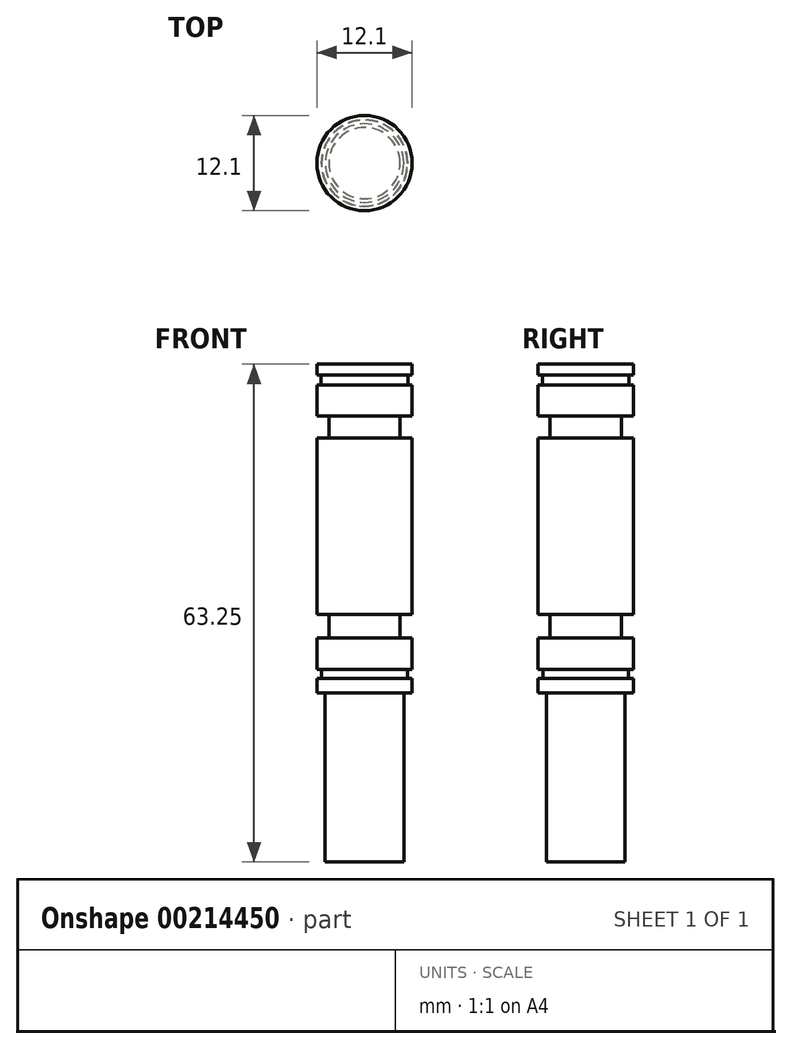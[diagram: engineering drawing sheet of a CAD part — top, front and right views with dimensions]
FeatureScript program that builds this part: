
annotation { "Feature Type Name" : "Feature", "Feature Type Description" : "" }
export const myFeature = defineFeature(function(context is Context, id is Id, definition is map)
    precondition{}
    {
        {
            var Q0;
            Q0=qCreatedBy(makeId("Top.planeOp"),FACE);
            var sketch = newSketch(context, id + "F0", { "sketchPlane" : qUnion([Q0])});
            skCircle(sketch, "E0", {"center": v(0, 0) * mm, "radius": 5 * mm});
            skSolve(sketch);
        }
        {
            var Q0;
            Q0=makeQuery(id+"F0.imprint","IMPRINT",FACE,{"disambiguationData":[TD([[makeQuery(id+"F0.imprint","IMPRINT",EDGE,{"derivedFrom":sQuery(id+"F0.wireOp",EDGE,"E0")}),1.0]])]});
            extrude(context, id + "F1", {"entities" : qUnion([Q0]), "oppositeDirection" : true, "depth" : 21.5 * mm});
        }
        {
            var Q0;
            Q0=qCreatedBy(makeId("Top.planeOp"),FACE);
            var sketch = newSketch(context, id + "F2", { "sketchPlane" : qUnion([Q0])});
            skCircle(sketch, "E1", {"center": v(0, 0) * mm, "radius": 6.05 * mm});
            skSolve(sketch);
        }
        {
            var Q0;
            Q0=makeQuery(id+"F2.imprint","IMPRINT",FACE,{"disambiguationData":[TD([[makeQuery(id+"F2.imprint","IMPRINT",EDGE,{"derivedFrom":sQuery(id+"F2.wireOp",EDGE,"E1")}),1.0]])]});
            var Q1;
            Q1=sQuery(id+"F2.wireOp",EDGE,"E1");
            extrude(context, id + "F3", {"entities" : qUnion([Q0]), "operationType" : NewBodyOperationType.ADD, "surfaceEntities" : qUnion([Q1]), "depth" : 1.8 * mm});
        }
        {
            var Q0;
            Q0=makeQuery(id+"F3.opExtrude","CAP_FACE",FACE,{"disambiguationData":[OSD([sQuery(id+"F2.wireOp",EDGE,"E1")])],"isStart":false});
            var sketch = newSketch(context, id + "F4", { "sketchPlane" : qUnion([Q0])});
            skCircle(sketch, "E2", {"center": v(0, 0) * mm, "radius": 5.45 * mm});
            skSolve(sketch);
        }
        {
            var Q0;
            Q0 = qSketchRegion(id + "F4", true);
            extrude(context, id + "F5", {"entities" : qUnion([Q0]), "operationType" : NewBodyOperationType.ADD, "depth" : 1.2 * mm});
        }
        {
            var Q0;
            Q0=makeQuery(id+"F5.opExtrude","CAP_FACE",FACE,{"disambiguationData":[OSD([sQuery(id+"F4.wireOp",EDGE,"E2")])],"isStart":false});
            var sketch = newSketch(context, id + "F6", { "sketchPlane" : qUnion([Q0])});
            skCircle(sketch, "E3", {"center": v(0, 0) * mm, "radius": 6.05 * mm});
            skSolve(sketch);
        }
        {
            var Q0;
            Q0 = qSketchRegion(id + "F6", true);
            extrude(context, id + "F7", {"entities" : qUnion([Q0]), "operationType" : NewBodyOperationType.ADD, "depth" : 3.95 * mm});
        }
        {
            var Q0;
            Q0=makeQuery(id+"F7.opExtrude","CAP_FACE",FACE,{"disambiguationData":[OSD([sQuery(id+"F6.wireOp",EDGE,"E3")])],"isStart":false});
            var sketch = newSketch(context, id + "F8", { "sketchPlane" : qUnion([Q0])});
            skCircle(sketch, "E4", {"center": v(0, 0) * mm, "radius": 4.53 * mm});
            skSolve(sketch);
        }
        {
            var Q0;
            Q0 = qSketchRegion(id + "F8", true);
            extrude(context, id + "F9", {"entities" : qUnion([Q0]), "operationType" : NewBodyOperationType.ADD, "depth" : 3 * mm});
        }
        {
            var Q0;
            Q0=makeQuery(id+"F9.opExtrude","CAP_FACE",FACE,{"disambiguationData":[OSD([sQuery(id+"F8.wireOp",EDGE,"E4")])],"isStart":false});
            var sketch = newSketch(context, id + "F10", { "sketchPlane" : qUnion([Q0])});
            skCircle(sketch, "E5", {"center": v(0, 0) * mm, "radius": 6.05 * mm});
            skSolve(sketch);
        }
        {
            var Q0;
            Q0 = qSketchRegion(id + "F10", true);
            extrude(context, id + "F11", {"entities" : qUnion([Q0]), "operationType" : NewBodyOperationType.ADD, "depth" : 22.45 * mm});
        }
        {
            var Q0;
            Q0=makeQuery(id+"F11.opExtrude","CAP_FACE",FACE,{"disambiguationData":[OSD([sQuery(id+"F10.wireOp",EDGE,"E5")])],"isStart":false});
            var sketch = newSketch(context, id + "F12", { "sketchPlane" : qUnion([Q0])});
            skCircle(sketch, "E6", {"center": v(0, 0) * mm, "radius": 4.53 * mm});
            skSolve(sketch);
        }
        {
            var Q0;
            Q0 = qSketchRegion(id + "F12", true);
            extrude(context, id + "F13", {"entities" : qUnion([Q0]), "operationType" : NewBodyOperationType.ADD, "depth" : 2.75 * mm});
        }
        {
            var Q0;
            Q0=makeQuery(id+"F13.opExtrude","CAP_FACE",FACE,{"disambiguationData":[OSD([sQuery(id+"F12.wireOp",EDGE,"E6")])],"isStart":false});
            var sketch = newSketch(context, id + "F14", { "sketchPlane" : qUnion([Q0])});
            skCircle(sketch, "E7", {"center": v(0, 0) * mm, "radius": 6.05 * mm});
            skSolve(sketch);
        }
        {
            var Q0;
            Q0 = qSketchRegion(id + "F14", true);
            extrude(context, id + "F15", {"entities" : qUnion([Q0]), "operationType" : NewBodyOperationType.ADD, "depth" : 3.95 * mm});
        }
        {
            var Q0;
            Q0=makeQuery(id+"F15.opExtrude","CAP_FACE",FACE,{"disambiguationData":[OSD([sQuery(id+"F14.wireOp",EDGE,"E7")])],"isStart":false});
            var sketch = newSketch(context, id + "F16", { "sketchPlane" : qUnion([Q0])});
            skCircle(sketch, "E8", {"center": v(0, 0) * mm, "radius": 5.5 * mm});
            skSolve(sketch);
        }
        {
            var Q0;
            Q0 = qSketchRegion(id + "F16", true);
            extrude(context, id + "F17", {"entities" : qUnion([Q0]), "operationType" : NewBodyOperationType.ADD, "depth" : 1.25 * mm});
        }
        {
            var Q0;
            Q0=makeQuery(id+"F17.opExtrude","CAP_FACE",FACE,{"disambiguationData":[OSD([sQuery(id+"F16.wireOp",EDGE,"E8")])],"isStart":false});
            var sketch = newSketch(context, id + "F18", { "sketchPlane" : qUnion([Q0])});
            skCircle(sketch, "E9", {"center": v(0, 0) * mm, "radius": 6.05 * mm});
            skSolve(sketch);
        }
        {
            var Q0;
            Q0 = qSketchRegion(id + "F18", true);
            extrude(context, id + "F19", {"entities" : qUnion([Q0]), "operationType" : NewBodyOperationType.ADD, "depth" : 1.4 * mm});
        }
    });
